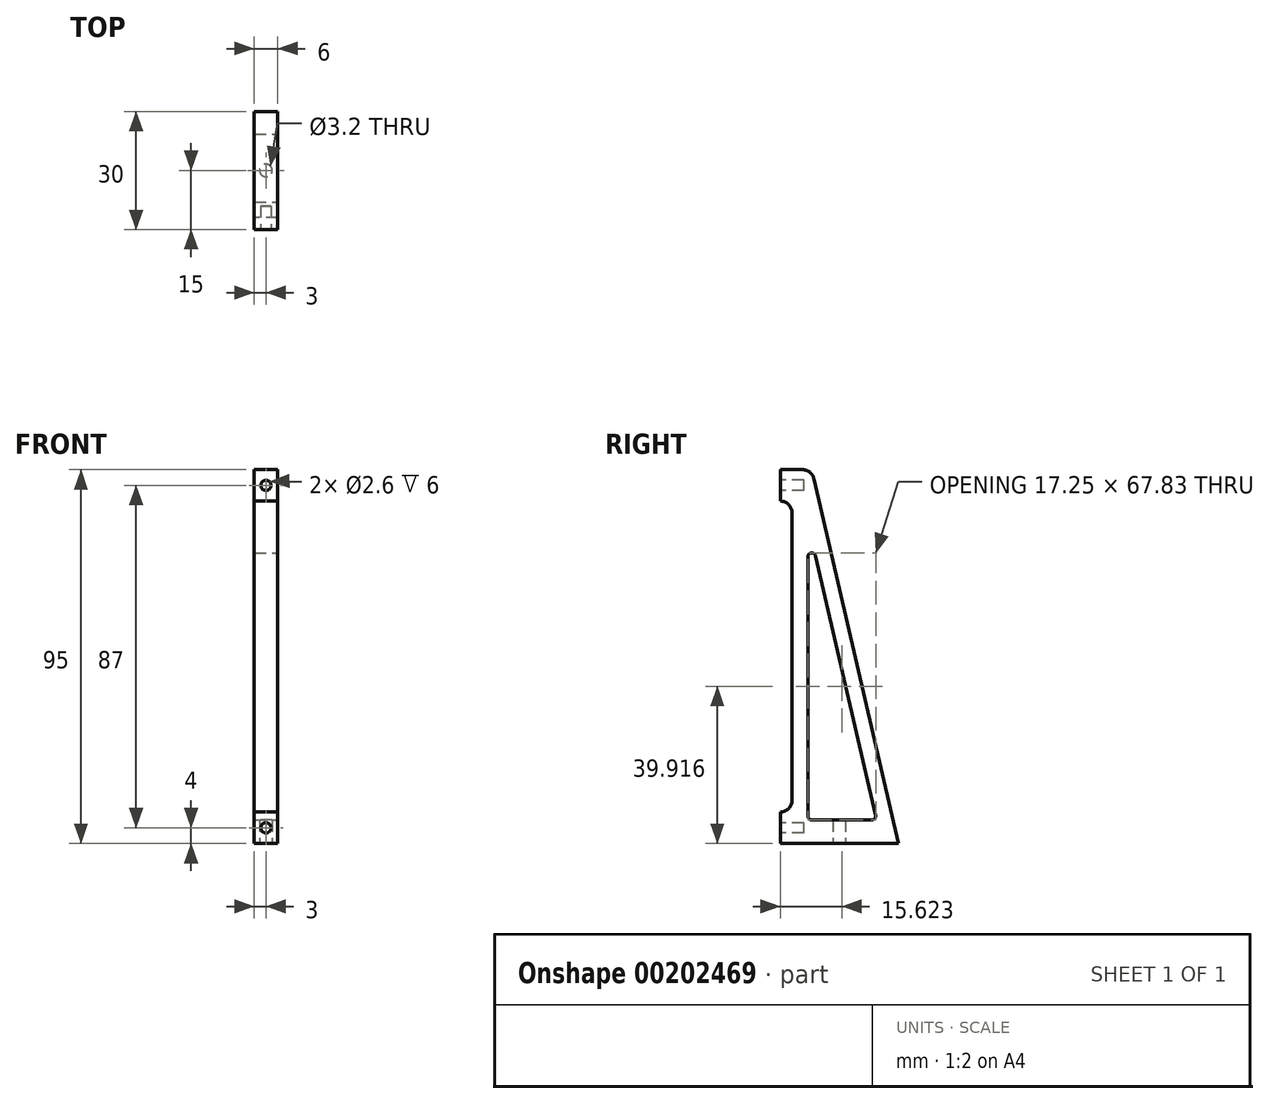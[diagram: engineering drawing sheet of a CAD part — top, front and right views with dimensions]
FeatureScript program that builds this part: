
annotation { "Feature Type Name" : "Feature", "Feature Type Description" : "" }
export const myFeature = defineFeature(function(context is Context, id is Id, definition is map)
    precondition{}
    {
        {
            var Q0;
            Q0=qCreatedBy(makeId("Right.planeOp"),FACE);
            var sketch = newSketch(context, id + "F0", { "sketchPlane" : qUnion([Q0])});
            skLineSegment(sketch, "E0", {"start": v(0, 0) * mm, "end": v(30, 0) * mm});
            skLineSegment(sketch, "E1", {"start": v(0, 0) * mm, "end": v(0, 8) * mm});
            skLineSegment(sketch, "E2", {"start": v(0, 8) * mm, "end": v(0, 8) * mm});
            skLineSegment(sketch, "E3", {"start": v(3, 11) * mm, "end": v(3, 84) * mm});
            skLineSegment(sketch, "E4", {"start": v(0, 87) * mm, "end": v(0, 87) * mm});
            skLineSegment(sketch, "E5", {"start": v(0, 87) * mm, "end": v(0, 95) * mm});
            skLineSegment(sketch, "E6", {"start": v(0, 95) * mm, "end": v(5.62, 95) * mm});
            skLineSegment(sketch, "E7", {"start": v(8.54, 92.68) * mm, "end": v(30, 0) * mm});
            skLineSegment(sketch, "E8", {"start": v(0, 91) * mm, "end": v(8.93, 91) * mm, "construction": true});
            skLineSegment(sketch, "E9", {"start": v(0, 4) * mm, "end": v(29.07, 4) * mm, "construction": true});
            skPoint(sketch, "E10.visualSharp", {"position": v(8, 95) * mm});
            skArc(sketch, "E10.filletArc", {"start": v(8.54, 92.68) * mm, "mid": v(7.48, 94.35) * mm, "end": v(5.62, 95) * mm});
            skPoint(sketch, "E11.visualSharp", {"position": v(3, 87) * mm});
            skArc(sketch, "E11.filletArc", {"start": v(3, 84) * mm, "mid": v(2.12, 86.12) * mm, "end": v(0, 87) * mm});
            skPoint(sketch, "E12.visualSharp", {"position": v(3, 8) * mm});
            skArc(sketch, "E12.filletArc", {"start": v(0, 8) * mm, "mid": v(2.12, 8.88) * mm, "end": v(3, 11) * mm});
            skSolve(sketch);
        }
        {
            var Q0;
            Q0=qSketchRegion(id+"F0",true);
            extrude(context, id + "F1", {"entities" : qUnion([Q0]), "depth" : 3 * mm, "hasSecondDirection" : true, "secondDirectionOppositeDirection" : true, "secondDirectionDepth" : 3 * mm});
        }
        {
            var Q0;
            Q0=qCreatedBy(makeId("Right.planeOp"),FACE);
            var sketch = newSketch(context, id + "F2", { "sketchPlane" : qUnion([Q0])});
            skLineSegment(sketch, "E13", {"start": v(8.97, 73.06) * mm, "end": v(24.22, 7.23) * mm});
            skLineSegment(sketch, "E14", {"start": v(23.25, 6) * mm, "end": v(8, 6) * mm});
            skLineSegment(sketch, "E15", {"start": v(7, 7) * mm, "end": v(7, 72.84) * mm});
            skPoint(sketch, "E16.visualSharp", {"position": v(7, 81.59) * mm});
            skArc(sketch, "E16.filletArc", {"start": v(8.97, 73.06) * mm, "mid": v(7.89, 73.83) * mm, "end": v(7, 72.84) * mm});
            skPoint(sketch, "E17.visualSharp", {"position": v(7, 6) * mm});
            skArc(sketch, "E17.filletArc", {"start": v(7, 7) * mm, "mid": v(7.3, 6.3) * mm, "end": v(8, 6) * mm});
            skPoint(sketch, "E18.visualSharp", {"position": v(24.5, 6) * mm});
            skArc(sketch, "E18.filletArc", {"start": v(23.25, 6) * mm, "mid": v(24.03, 6.38) * mm, "end": v(24.22, 7.23) * mm});
            skSolve(sketch);
        }
        {
            var Q0;
            Q0=qSketchRegion(id+"F2",true);
            extrude(context, id + "F3", {"entities" : qUnion([Q0]), "operationType" : NewBodyOperationType.REMOVE, "endBound" : BoundingType.UP_TO_NEXT, "oppositeDirection" : true, "depth" : 25 * mm, "hasSecondDirection" : true, "secondDirectionBound" : SecondDirectionBoundingType.UP_TO_NEXT, "secondDirectionOppositeDirection" : false, "secondDirectionDepth" : 25 * mm});
        }
        {
            var Q0;
            Q0=makeQuery(id+"F1.opExtrude","SWEPT_FACE",FACE,{"disambiguationData":[OSD([sQuery(id+"F0.wireOp",EDGE,"E5")])]});
            var sketch = newSketch(context, id + "F4", { "sketchPlane" : qUnion([Q0])});
            skCircle(sketch, "E19", {"center": v(0, 91) * mm, "radius": 1.3 * mm});
            skCircle(sketch, "E20", {"center": v(0, 4) * mm, "radius": 1.3 * mm});
            skSolve(sketch);
        }
        {
            var Q0;
            Q0=qSketchRegion(id+"F4",true);
            extrude(context, id + "F5", {"entities" : qUnion([Q0]), "operationType" : NewBodyOperationType.REMOVE, "oppositeDirection" : true, "depth" : 6 * mm});
        }
        {
            var Q0;
            Q0=makeQuery(id+"F1.opExtrude","SWEPT_FACE",FACE,{"disambiguationData":[OSD([sQuery(id+"F0.wireOp",EDGE,"E0")])]});
            var sketch = newSketch(context, id + "F6", { "sketchPlane" : qUnion([Q0])});
            skCircle(sketch, "E21", {"center": v(0, -15) * mm, "radius": 1.6 * mm});
            skSolve(sketch);
        }
        {
            var Q0;
            Q0=qSketchRegion(id+"F6",true);
            extrude(context, id + "F7", {"entities" : qUnion([Q0]), "operationType" : NewBodyOperationType.REMOVE, "endBound" : BoundingType.UP_TO_NEXT, "oppositeDirection" : true, "depth" : 25 * mm});
        }
    });
